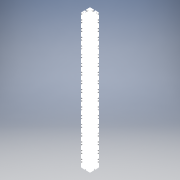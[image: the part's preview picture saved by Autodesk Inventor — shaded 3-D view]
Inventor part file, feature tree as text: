
AUTODESK INVENTOR PART (.ipt)
format: ipt  version: 2018 (Build 220112000, 112)  size: 594,432 bytes
history: native  units: mm
features: other x1, extrude x1, sketch x1
ambient origin geometry x8: Origin, YZ Plane, XZ Plane, XY Plane, X Axis, Y Axis, Z Axis, Center Point
bodies: Body1 (feature_tree)
feature tree (3):
  other  "Sólido1"
  extrude  "Extrusão1"  [1 undecoded]
  sketch  "Esboço1"  dims[d0=615.0mm d1=0.0mm]
note: 1 required parameter value undecoded (feature->parameter linkage not recoverable at this tier; creation-order binding heuristic only, values carry confidence <= 0.55)
